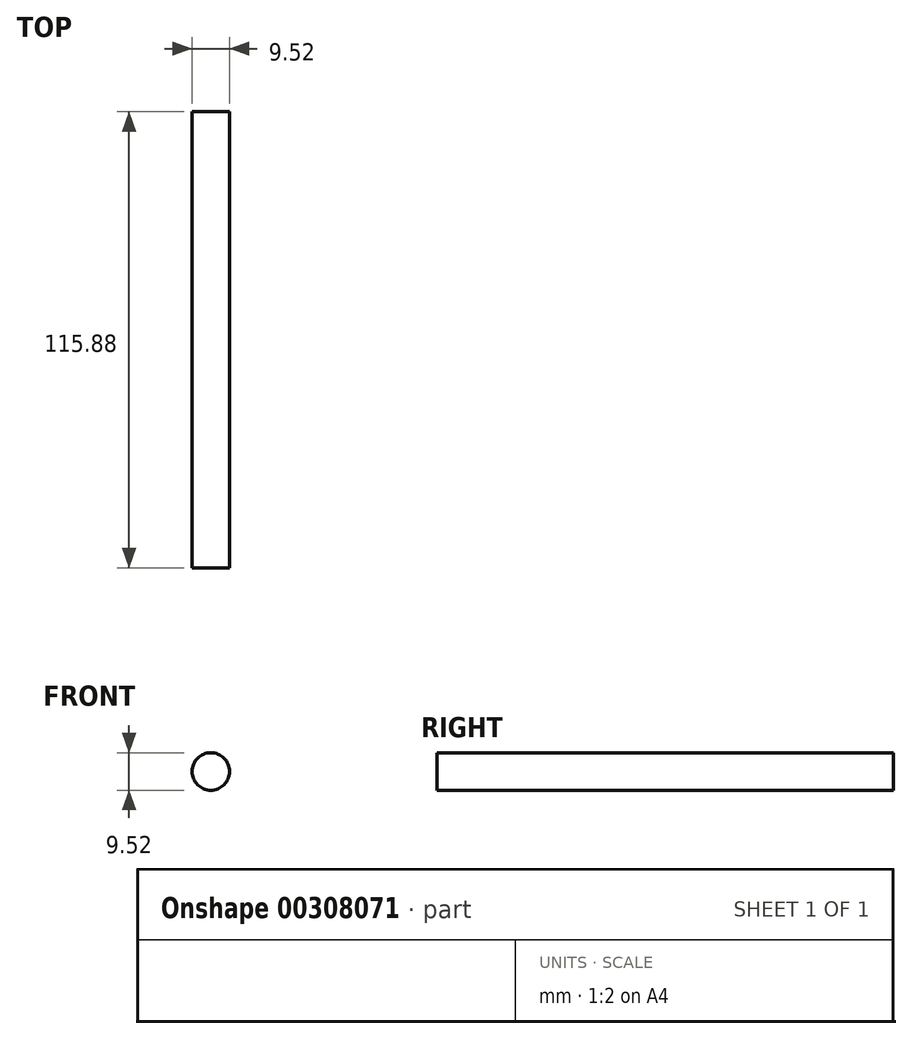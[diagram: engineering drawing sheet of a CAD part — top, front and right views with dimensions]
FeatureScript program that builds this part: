
annotation { "Feature Type Name" : "Feature", "Feature Type Description" : "" }
export const myFeature = defineFeature(function(context is Context, id is Id, definition is map)
    precondition{}
    {
        {
            var Q0;
            Q0=qCreatedBy(makeId("Front.planeOp"),FACE);
            var sketch = newSketch(context, id + "F0", { "sketchPlane" : qUnion([Q0])});
            skCircle(sketch, "E0", {"center": v(0, 0) * mm, "radius": 4.76 * mm});
            skSolve(sketch);
        }
        {
            var Q0;
            Q0 = qSketchRegion(id + "F0", true);
            extrude(context, id + "F1", {"entities" : qUnion([Q0]), "endBound" : BoundingType.SYMMETRIC, "depth" : 115.89 * mm, "offsetDistance" : 25.4 * mm});
        }
    });
